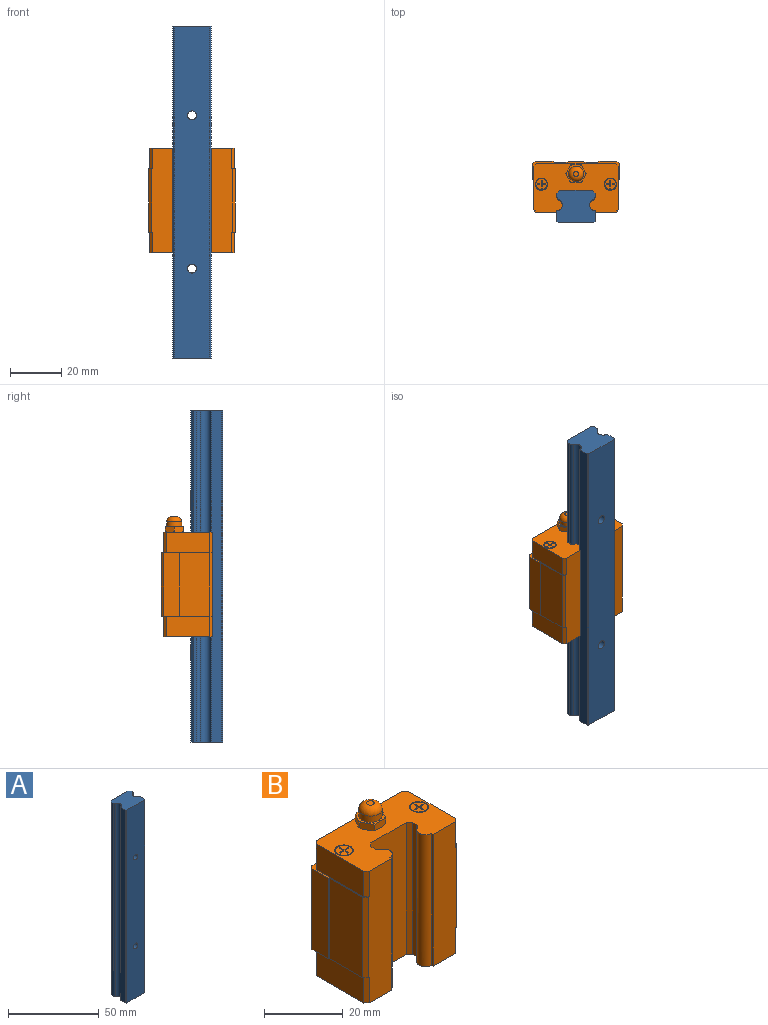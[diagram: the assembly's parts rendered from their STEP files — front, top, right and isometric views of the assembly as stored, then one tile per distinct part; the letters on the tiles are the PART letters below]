
ASSEMBLY  parts=2 mates=1
PART A: 22 faces, bbox 15x12.5x130 mm
  f0: cylinder r=1.75mm len=8mm, axis (0,-1,0), area 88mm2, adj f1,f11
  f1: plane 6.01x6.01mm, normal (0,1,0), area 18.7mm2, adj f0,f14
  f2: plane 130x4.01mm, normal (1,0,0), area 520.6mm2, adj f3,f12,f16,f18
  f3: cylinder r=2.2mm len=130mm, axis (0,0,-1), area 779.1mm2, adj f2,f4,f16,f18
  f4: cylinder r=1.5mm len=130mm, axis (0,0,-1), area 224.9mm2, adj f3,f5,f16,f18
  f5: plane 130x1.29mm, normal (1,0,0), area 167.5mm2, adj f4,f15,f16,f18
  f6: plane 130x1.29mm, normal (-1,0,0), area 167.5mm2, adj f7,f16,f17,f18
  f7: cylinder r=1.5mm len=130mm, axis (0,0,-1), area 224.9mm2, adj f6,f8,f16,f18
  f8: cylinder r=2.2mm len=130mm, axis (0,0,-1), area 779.1mm2, adj f7,f9,f16,f18
  f9: plane 130x4.01mm, normal (-1,0,0), area 520.6mm2, adj f8,f10,f16,f18
  f10: plane 130x0.5mm, normal (-0.71,-0.71,0), area 91.9mm2, adj f9,f11,f16,f18
  f11: plane 130x14mm, normal (0,-1,0), area 1800.8mm2, adj f0,f10,f12,f13,f16,f18
  f12: plane 130x0.5mm, normal (0.71,-0.71,0), area 91.9mm2, adj f2,f11,f16,f18
  f13: cylinder r=1.75mm len=8mm, axis (0,-1,0), area 88mm2, adj f11,f19
  f14: cylinder r=3mm len=6mm, axis (0,-1,0), area 84.8mm2, adj f1,f20
  f15: plane 130x1.12mm, normal (0.71,0.71,0), area 206.7mm2, adj f5,f16,f18,f20
  f16: plane 15x12.5mm, normal (0,0,1), area 170.3mm2, adj f2,f3,f4,f5,f6,f7,f8,f9
  f17: plane 130x1.12mm, normal (-0.71,0.71,0), area 206.7mm2, adj f6,f16,f18,f20
  f18: plane 15x12.5mm, normal (0,0,-1), area 170.3mm2, adj f2,f3,f4,f5,f6,f7,f8,f9
  f19: plane 6x6mm, normal (0,1,0), area 18.7mm2, adj f13,f21
  f20: plane 130.01x12.76mm, normal (0,1,0), area 1601.1mm2, adj f14,f15,f16,f17,f18,f21
  f21: cylinder r=3mm len=6mm, axis (0,-1,0), area 84.8mm2, adj f19,f20
PART B: 146 faces, bbox 34.1x20.1x47.1 mm
  f0: plane 3.09x3.09mm, normal (0,0,-1), area 2.3mm2, adj f2,f3,f4,f5,f6,f7,f8,f9
  f1: plane 3.08x3.08mm, normal (0,0,-1), area 2.3mm2, adj f14,f15,f16,f17,f18,f19,f20,f21
  f2: plane 1.33x0.2mm, normal (0,1,0), area 0.3mm2, adj f0,f3,f13,f28
  f3: cylinder r=1.54mm len=0.4mm, axis (0,0,1), area 0.1mm2, adj f0,f2,f4,f28
  f4: plane 1.33x0.2mm, normal (0,-1,0), area 0.3mm2, adj f0,f3,f5,f28
  f5: plane 1.33x0.2mm, normal (1,0,0), area 0.3mm2, adj f0,f4,f6,f28
  f6: cylinder r=1.54mm len=0.4mm, axis (0,0,1), area 0.1mm2, adj f0,f5,f7,f28
  f7: plane 1.33x0.2mm, normal (-1,0,0), area 0.3mm2, adj f0,f6,f8,f28
  f8: plane 1.33x0.2mm, normal (0,-1,0), area 0.3mm2, adj f0,f7,f9,f28
  f9: cylinder r=1.54mm len=0.4mm, axis (0,0,1), area 0.1mm2, adj f0,f8,f10,f28
  f10: plane 1.33x0.2mm, normal (0,1,0), area 0.3mm2, adj f0,f9,f11,f28
  f11: plane 1.33x0.2mm, normal (-1,0,0), area 0.3mm2, adj f0,f10,f12,f28
  f12: cylinder r=1.54mm len=0.4mm, axis (0,0,1), area 0.1mm2, adj f0,f11,f13,f28
  f13: plane 1.33x0.2mm, normal (1,0,0), area 0.3mm2, adj f0,f2,f12,f28
  f14: plane 1.33x0.2mm, normal (0,-1,0), area 0.3mm2, adj f1,f15,f25,f29
  f15: cylinder r=1.54mm len=0.4mm, axis (0,0,1), area 0.1mm2, adj f1,f14,f16,f29
  f16: plane 1.33x0.2mm, normal (0,1,0), area 0.3mm2, adj f1,f15,f17,f29
  f17: plane 1.33x0.2mm, normal (-1,0,0), area 0.3mm2, adj f1,f16,f18,f29
  f18: cylinder r=1.54mm len=0.4mm, axis (0,0,1), area 0.1mm2, adj f1,f17,f19,f29
  f19: plane 1.33x0.2mm, normal (1,0,0), area 0.3mm2, adj f1,f18,f20,f29
  f20: plane 1.33x0.2mm, normal (0,1,0), area 0.3mm2, adj f1,f19,f21,f29
  f21: cylinder r=1.54mm len=0.4mm, axis (0,0,1), area 0.1mm2, adj f1,f20,f22,f29
  f22: plane 1.33x0.2mm, normal (0,-1,0), area 0.3mm2, adj f1,f21,f23,f29
  f23: plane 1.33x0.2mm, normal (1,0,0), area 0.3mm2, adj f1,f22,f24,f29
  f24: cylinder r=1.54mm len=0.4mm, axis (0,0,1), area 0.1mm2, adj f1,f23,f25,f29
  f25: plane 1.33x0.2mm, normal (-1,0,0), area 0.3mm2, adj f1,f14,f24,f29
  f26: plane 3.08x3.08mm, normal (0,0,1), area 2.3mm2, adj f32,f33,f34,f35,f36,f37,f38,f39
  f27: plane 3.09x3.09mm, normal (0,0,1), area 2.3mm2, adj f44,f45,f46,f47,f48,f49,f50,f51
  f28: plane 4.4x4.4mm, normal (0,0,-1), area 12.9mm2, adj f2,f3,f4,f5,f6,f7,f8,f9
  f29: plane 4.4x4.4mm, normal (0,0,-1), area 12.9mm2, adj f14,f15,f16,f17,f18,f19,f20,f21
  f30: cone r=1.62mm half-angle=60deg, axis (0,1,0), area 9.5mm2, adj f58
  f31: cone r=1.62mm half-angle=60deg, axis (0,1,0), area 9.5mm2, adj f59
  f32: plane 1.33x0.2mm, normal (1,0,0), area 0.3mm2, adj f26,f33,f43,f60
  f33: plane 1.33x0.2mm, normal (0,1,0), area 0.3mm2, adj f26,f32,f34,f60
  f34: cylinder r=1.54mm len=0.4mm, axis (0,0,1), area 0.1mm2, adj f26,f33,f35,f60
  f35: plane 1.33x0.2mm, normal (0,-1,0), area 0.3mm2, adj f26,f34,f36,f60
  f36: plane 1.33x0.2mm, normal (1,0,0), area 0.3mm2, adj f26,f35,f37,f60
  f37: cylinder r=1.54mm len=0.4mm, axis (0,0,1), area 0.1mm2, adj f26,f36,f38,f60
  f38: plane 1.33x0.2mm, normal (-1,0,0), area 0.3mm2, adj f26,f37,f39,f60
  f39: plane 1.33x0.2mm, normal (0,-1,0), area 0.3mm2, adj f26,f38,f40,f60
  f40: cylinder r=1.54mm len=0.4mm, axis (0,0,1), area 0.1mm2, adj f26,f39,f41,f60
  f41: plane 1.33x0.2mm, normal (0,1,0), area 0.3mm2, adj f26,f40,f42,f60
  f42: plane 1.33x0.2mm, normal (-1,0,0), area 0.3mm2, adj f26,f41,f43,f60
  f43: cylinder r=1.54mm len=0.4mm, axis (0,0,1), area 0.1mm2, adj f26,f32,f42,f60
  f44: plane 1.33x0.2mm, normal (1,0,0), area 0.3mm2, adj f27,f45,f55,f61
  f45: cylinder r=1.54mm len=0.4mm, axis (0,0,1), area 0.1mm2, adj f27,f44,f46,f61
  f46: plane 1.33x0.2mm, normal (-1,0,0), area 0.3mm2, adj f27,f45,f47,f61
  f47: plane 1.33x0.2mm, normal (0,-1,0), area 0.3mm2, adj f27,f46,f48,f61
  f48: cylinder r=1.54mm len=0.4mm, axis (0,0,1), area 0.1mm2, adj f27,f47,f49,f61
  f49: plane 1.33x0.2mm, normal (0,1,0), area 0.3mm2, adj f27,f48,f50,f61
  f50: plane 1.33x0.2mm, normal (-1,0,0), area 0.3mm2, adj f27,f49,f51,f61
  f51: cylinder r=1.54mm len=0.4mm, axis (0,0,1), area 0.1mm2, adj f27,f50,f52,f61
  f52: plane 1.33x0.2mm, normal (1,0,0), area 0.3mm2, adj f27,f51,f53,f61
  f53: plane 1.33x0.2mm, normal (0,1,0), area 0.3mm2, adj f27,f52,f54,f61
  f54: cylinder r=1.54mm len=0.4mm, axis (0,0,1), area 0.1mm2, adj f27,f53,f55,f61
  f55: plane 1.33x0.2mm, normal (0,-1,0), area 0.3mm2, adj f27,f44,f54,f61
  f56: cylinder r=2.2mm len=4.4mm, axis (0,0,-1), area 34.6mm2, adj f28,f62
  f57: cylinder r=2.2mm len=4.4mm, axis (0,0,-1), area 34.6mm2, adj f29,f63
  f58: cylinder r=1.62mm len=9.69mm, axis (0,-1,0), area 98.6mm2, adj f30,f64
  f59: cylinder r=1.62mm len=9.69mm, axis (0,-1,0), area 98.6mm2, adj f31,f65
  f60: plane 4.4x4.4mm, normal (0,0,1), area 12.9mm2, adj f32,f33,f34,f35,f36,f37,f38,f39
  f61: plane 4.4x4.4mm, normal (0,0,1), area 12.9mm2, adj f44,f45,f46,f47,f48,f49,f50,f51
  f62: plane 4.8x4.8mm, normal (0,0,-1), area 2.9mm2, adj f56,f68
  f63: plane 4.8x4.8mm, normal (0,0,-1), area 2.9mm2, adj f57,f69
  f64: cone r=2mm half-angle=45deg, axis (0,1,0), area 6.1mm2, adj f58,f79
  f65: cone r=2mm half-angle=45deg, axis (0,1,0), area 6.1mm2, adj f59,f87
  f66: cylinder r=2.2mm len=4.4mm, axis (0,0,-1), area 34.6mm2, adj f60,f92
  f67: cylinder r=2.2mm len=4.4mm, axis (0,0,-1), area 34.6mm2, adj f61,f93
  f68: cylinder r=2.4mm len=4.8mm, axis (0,0,-1), area 37.7mm2, adj f62,f97
  f69: cylinder r=2.4mm len=4.8mm, axis (0,0,1), area 37.7mm2, adj f63,f97
  f70: plane 17.01x8mm, normal (1,0,0), area 136.1mm2, adj f71,f95,f97,f99
  f71: plane 8x0.99mm, normal (0.71,0.71,0), area 11.2mm2, adj f70,f72,f97,f99
  f72: plane 30.92x8mm, normal (0,1,0), area 247.4mm2, adj f71,f73,f97,f99
  f73: plane 8x0.99mm, normal (-0.71,0.71,0), area 11.2mm2, adj f72,f74,f97,f99
  f74: plane 17.01x8mm, normal (-1,0,0), area 136.1mm2, adj f73,f97,f98,f99
  f75: plane 25x12mm, normal (-1,0,0), area 300.1mm2, adj f76,f96,f99,f100
  f76: plane 25x0.25mm, normal (0,-1,0), area 6.3mm2, adj f75,f77,f99,f100
  f77: plane 25x6mm, normal (-1,0,0), area 150mm2, adj f76,f78,f99,f100
  f78: plane 25x1mm, normal (-0.71,0.71,0), area 35.4mm2, adj f77,f79,f99,f100
  f79: plane 25x7mm, normal (0,1,0), area 162.4mm2, adj f64,f78,f80,f99,f100
  f80: plane 25x0.5mm, normal (0.71,0.71,0), area 17.7mm2, adj f79,f81,f99,f100
  f81: plane 25x5mm, normal (0,1,0), area 125mm2, adj f80,f82,f99,f100
  f82: plane 25x0.5mm, normal (-0.71,0.71,0), area 17.7mm2, adj f81,f83,f99,f100
  f83: plane 25x6mm, normal (0,1,0), area 150mm2, adj f82,f84,f99,f100
  f84: plane 25x0.5mm, normal (0.71,0.71,0), area 17.7mm2, adj f83,f85,f99,f100
  f85: plane 25x5mm, normal (0,1,0), area 125mm2, adj f84,f86,f99,f100
  f86: plane 25x0.5mm, normal (-0.71,0.71,0), area 17.7mm2, adj f85,f87,f99,f100
  f87: plane 25x7mm, normal (0,1,0), area 162.4mm2, adj f65,f86,f88,f99,f100
  f88: plane 25x1mm, normal (0.71,0.71,0), area 35.4mm2, adj f87,f89,f99,f100
  f89: plane 25x6mm, normal (1,0,0), area 150mm2, adj f88,f90,f99,f100
  f90: plane 25x0.25mm, normal (0,-1,0), area 6.3mm2, adj f89,f91,f99,f100
  f91: plane 25x12mm, normal (1,0,0), area 300.1mm2, adj f90,f94,f99,f100
  f92: plane 4.8x4.8mm, normal (0,0,1), area 2.9mm2, adj f66,f101
  f93: plane 4.8x4.8mm, normal (0,0,1), area 2.9mm2, adj f67,f102
  f94: plane 25x1mm, normal (0.71,-0.71,0), area 35.3mm2, adj f91,f99,f100,f106
  f95: plane 8x1mm, normal (0.71,-0.71,0), area 11.3mm2, adj f70,f97,f99,f106
  f96: plane 25x1mm, normal (-0.71,-0.71,0), area 35.3mm2, adj f75,f99,f100,f118
  f97: plane 32.9x19mm, normal (0,0,-1), area 476.4mm2, adj f68,f69,f70,f71,f72,f73,f74,f95
  f98: plane 8x1mm, normal (-0.71,-0.71,0), area 11.3mm2, adj f74,f97,f99,f118
  f99: plane 34x20mm, normal (0,0,-1), area 42.9mm2, adj f70,f71,f72,f73,f74,f75,f76,f77
  f100: plane 34x20mm, normal (0,0,1), area 42.9mm2, adj f75,f76,f77,f78,f79,f80,f81,f82
  f101: cylinder r=2.4mm len=4.8mm, axis (0,0,1), area 37.7mm2, adj f92,f128
  f102: cylinder r=2.4mm len=4.8mm, axis (0,0,-1), area 37.7mm2, adj f93,f128
  f103: plane 8x0.99mm, normal (0.71,0.71,0), area 11.2mm2, adj f100,f104,f122,f128
  f104: plane 17.01x8mm, normal (1,0,0), area 136.1mm2, adj f100,f103,f105,f128
  f105: plane 8x1mm, normal (0.71,-0.71,0), area 11.3mm2, adj f100,f104,f106,f128
  f106: plane 41x8.25mm, normal (0,-1,0), area 333.6mm2, adj f94,f95,f97,f99,f100,f105,f107,f128
  f107: plane 41x0.51mm, normal (-1,0,0), area 20.7mm2, adj f97,f106,f108,f128
  f108: cylinder r=2.2mm len=41mm, axis (0,0,-1), area 245.7mm2, adj f97,f107,f109,f128
  f109: cylinder r=1.5mm len=41mm, axis (0,0,-1), area 70.9mm2, adj f97,f108,f110,f128
  f110: plane 41x1.29mm, normal (-1,0,0), area 52.8mm2, adj f97,f109,f111,f128
  f111: plane 41x1.12mm, normal (-0.71,-0.71,0), area 65.2mm2, adj f97,f110,f112,f128
  f112: plane 41x12.75mm, normal (0,-1,0), area 522.8mm2, adj f97,f111,f113,f128
  f113: plane 41x1.12mm, normal (0.71,-0.71,0), area 65.2mm2, adj f97,f112,f114,f128
  f114: plane 41x1.29mm, normal (1,0,0), area 52.8mm2, adj f97,f113,f115,f128
  f115: cylinder r=1.5mm len=41mm, axis (0,0,-1), area 70.9mm2, adj f97,f114,f116,f128
  f116: cylinder r=2.2mm len=41mm, axis (0,0,-1), area 245.7mm2, adj f97,f115,f117,f128
  f117: plane 41x0.51mm, normal (1,0,0), area 20.7mm2, adj f97,f116,f118,f128
  f118: plane 41x8.25mm, normal (0,-1,0), area 333.6mm2, adj f96,f97,f98,f99,f100,f117,f119,f128
  f119: plane 8x1mm, normal (-0.71,-0.71,0), area 11.3mm2, adj f100,f118,f120,f128
  f120: plane 17.01x8mm, normal (-1,0,0), area 136.1mm2, adj f100,f119,f121,f128
  f121: plane 8x0.99mm, normal (-0.71,0.71,0), area 11.2mm2, adj f100,f120,f122,f128
  f122: plane 30.92x8mm, normal (0,1,0), area 247.4mm2, adj f100,f103,f121,f128
  f123: cone r=4.04mm half-angle=45deg, axis (0,0,1), area 0.3mm2, adj f128,f130,f132
  f124: cone r=4.04mm half-angle=45deg, axis (0,0,1), area 0.3mm2, adj f128,f132,f134
  f125: cone r=4.04mm half-angle=45deg, axis (0,0,1), area 0.3mm2, adj f128,f134,f136
  f126: cone r=4.04mm half-angle=45deg, axis (0,0,1), area 0.3mm2, adj f128,f136,f138
  f127: cone r=4.04mm half-angle=45deg, axis (0,0,1), area 0.3mm2, adj f128,f130,f140
  f128: plane 32.9x19mm, normal (0,0,1), area 435.2mm2, adj f101,f102,f103,f104,f105,f106,f107,f108
  f129: cone r=4.04mm half-angle=45deg, axis (0,0,1), area 0.3mm2, adj f128,f138,f140
  f130: plane 3.55x2.12mm, normal (-0.87,0.5,0), area 7.9mm2, adj f123,f127,f128,f131,f132,f140,f141,f143
  f131: cone r=4.04mm half-angle=45deg, axis (0,0,-1), area 0.3mm2, adj f130,f132,f143
  f132: plane 3.55x2.12mm, normal (-0.87,-0.5,0), area 7.9mm2, adj f123,f124,f128,f130,f131,f133,f134,f143
  f133: cone r=4.04mm half-angle=45deg, axis (0,0,-1), area 0.3mm2, adj f132,f134,f143
  f134: plane 4.09x2.12mm, normal (0,-1,0), area 7.9mm2, adj f124,f125,f128,f132,f133,f135,f136,f143
  f135: cone r=4.04mm half-angle=45deg, axis (0,0,-1), area 0.3mm2, adj f134,f136,f143
  f136: plane 3.55x2.12mm, normal (0.87,-0.5,0), area 7.9mm2, adj f125,f126,f128,f134,f135,f137,f138,f143
  f137: cone r=4.04mm half-angle=45deg, axis (0,0,-1), area 0.3mm2, adj f136,f138,f143
  f138: plane 3.55x2.12mm, normal (0.87,0.5,0), area 7.9mm2, adj f126,f128,f129,f136,f137,f139,f140,f143
  f139: cone r=4.04mm half-angle=45deg, axis (0,0,-1), area 0.3mm2, adj f138,f140,f143
  f140: plane 4.09x2.12mm, normal (0,1,0), area 7.9mm2, adj f127,f128,f129,f130,f138,f139,f141,f143
  f141: cone r=4.04mm half-angle=45deg, axis (0,0,-1), area 0.3mm2, adj f130,f140,f143
  f142: plane 1.94x1.94mm, normal (0,0,1), area 3mm2, adj f144
  f143: plane 7.5x7mm, normal (0,0,1), area 13.6mm2, adj f130,f131,f132,f133,f134,f135,f136,f137
  f144: torus R=0.97mm, axis (0,0,1), area 44.3mm2, adj f142,f145
  f145: cylinder r=2.97mm len=5.94mm, axis (0,0,1), area 36mm2, adj f143,f144
PLACE A at identity fixed
PLACE B t=(0,4,-3.32)mm
MATE slider B.f108 <-> A.f3  axis (0,0,-1) through (7.5,6.7,-3.32)mm
